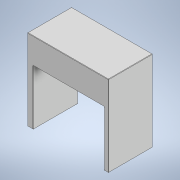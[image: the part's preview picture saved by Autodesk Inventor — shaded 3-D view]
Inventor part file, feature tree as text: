
AUTODESK INVENTOR PART (.ipt)
format: ipt  version: 2021 (Build 250183000, 183)  size: 168,960 bytes
history: native  units: in
note: dims shown in document units (in); Inventor stores cm internally (conversion verified against a paired STEP export)
features: extrude x4, sketch x4, fillet x1
ambient origin geometry x8: Origin, YZ Plane, XZ Plane, XY Plane, X Axis, Y Axis, Z Axis, Center Point
bodies: Solid1 (feature_tree)
feature tree (9):
  extrude  "Extrusion1"  Depth=23.622in
  extrude  "Extrusion2"  Depth=16.5354in
  extrude  "Extrusion3"  Depth=39.3701in TaperAngle=0.0deg
  extrude  "Extrusion4"  Depth=0.1969in TaperAngle=0.0deg
  fillet  "Fillet1"  Radius=5.9055in
  sketch  "Sketch1"  dims[d0=43.3071in d1=23.622in]
  sketch  "Sketch2"  dims[d2=43.3071in d3=0.0in d4=16.5354in]
  sketch  "Sketch3"  dims[d5=21.2598in d6=39.3701in d7=0.0in]
  sketch  "Sketch4"  dims[d8=16.5354in d9=5.9055in d10=0.0in d11=5.9055in d12=3.937in d13=0.0in d14=0.1969in d15=29.5276in]
